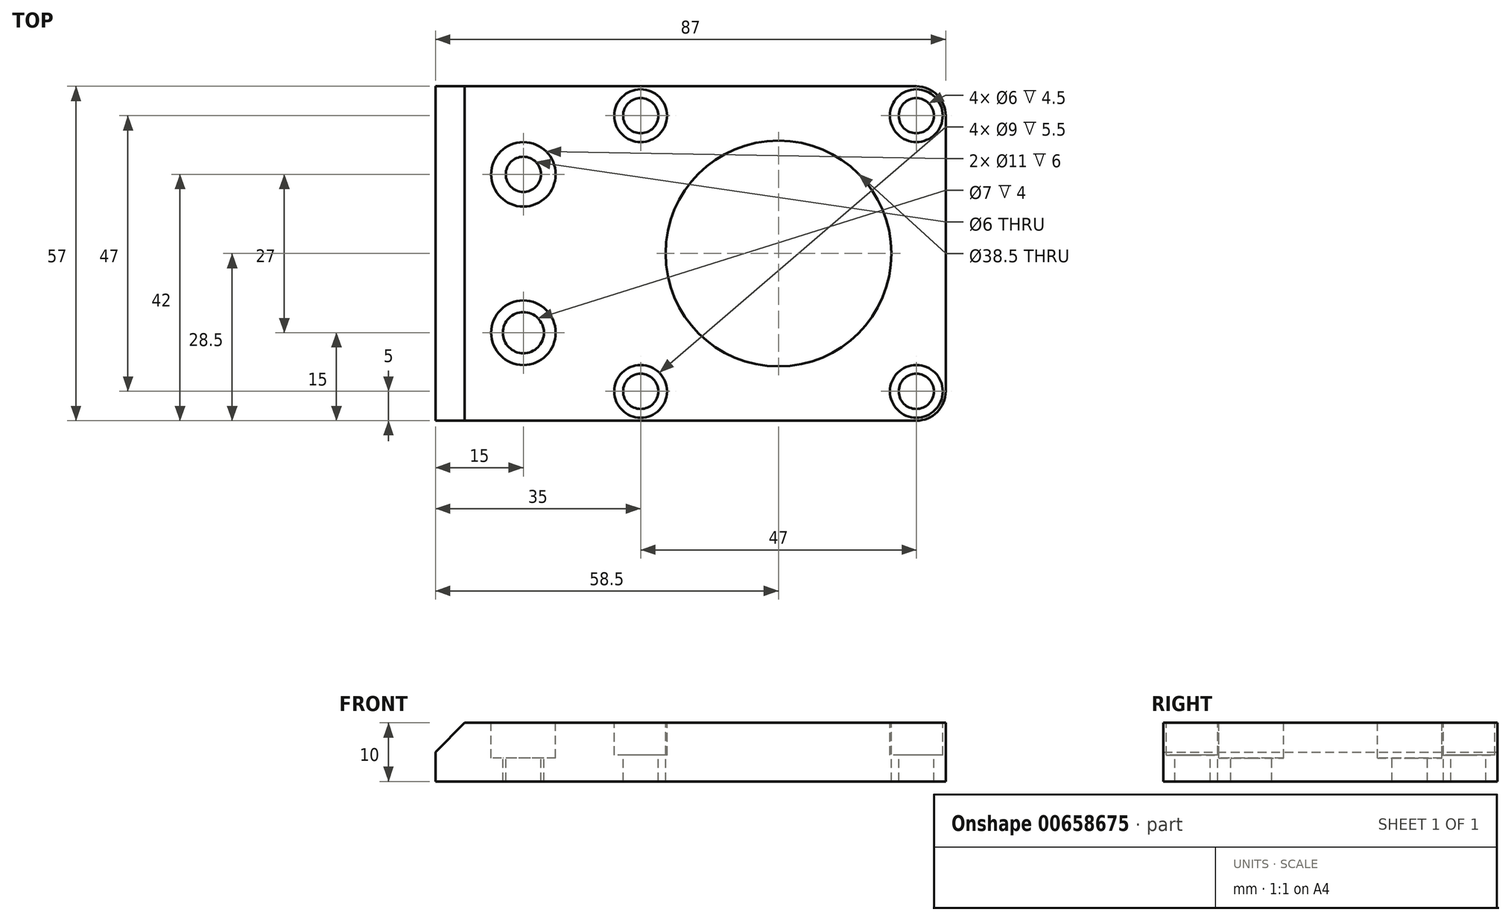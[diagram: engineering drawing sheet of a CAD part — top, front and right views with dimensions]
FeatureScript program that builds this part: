
annotation { "Feature Type Name" : "Feature", "Feature Type Description" : "" }
export const myFeature = defineFeature(function(context is Context, id is Id, definition is map)
    precondition{}
    {
        {
            var Q0;
            Q0=qCreatedBy(makeId("Top.planeOp"),FACE);
            var sketch = newSketch(context, id + "F0", { "sketchPlane" : qUnion([Q0])});
            skLineSegment(sketch, "E0.rect.bottom", {"start": v(43.5, -28.5) * mm, "end": v(-43.5, -28.5) * mm});
            skLineSegment(sketch, "E0.rect.top", {"start": v(43.5, 28.5) * mm, "end": v(-43.5, 28.5) * mm});
            skLineSegment(sketch, "E0.rect.left", {"start": v(43.5, -28.5) * mm, "end": v(43.5, 28.5) * mm});
            skLineSegment(sketch, "E0.rect.right", {"start": v(-43.5, -28.5) * mm, "end": v(-43.5, 28.5) * mm});
            skPoint(sketch, "E0.rect.middle", {"position": v(0, 0) * mm});
            skSolve(sketch);
        }
        {
            var Q0;
            Q0=makeQuery(id+"F0.imprint","IMPRINT",FACE,{"disambiguationData":[TD([[makeQuery(id+"F0.imprint","IMPRINT",EDGE,{"derivedFrom":sQuery(id+"F0.wireOp",EDGE,"E0.rect.bottom")}),-1.0]])]});
            extrude(context, id + "F1", {"entities" : qUnion([Q0]), "depth" : 10 * mm});
        }
        {
            var Q0;
            Q0=makeQuery(id+"F1.opExtrude","CAP_FACE",FACE,{"disambiguationData":[OSD([sQuery(id+"F0.wireOp",EDGE,"E0.rect.bottom"),sQuery(id+"F0.wireOp",EDGE,"E0.rect.top"),sQuery(id+"F0.wireOp",EDGE,"E0.rect.left"),sQuery(id+"F0.wireOp",EDGE,"E0.rect.right")])],"isStart":false});
            var sketch = newSketch(context, id + "F2", { "sketchPlane" : qUnion([Q0])});
            skCircle(sketch, "E1", {"center": v(15, 0) * mm, "radius": 19.25 * mm});
            skCircle(sketch, "E2", {"center": v(-28.5, -13.5) * mm, "radius": 3.5 * mm});
            skCircle(sketch, "E3", {"center": v(-28.5, 13.5) * mm, "radius": 3 * mm});
            skSolve(sketch);
        }
        {
            var Q0;
            Q0=makeQuery(id+"F2.imprint","IMPRINT",FACE,{"disambiguationData":[TD([[makeQuery(id+"F2.imprint","IMPRINT",EDGE,{"derivedFrom":sQuery(id+"F2.wireOp",EDGE,"E1")}),1.0]])]});
            var Q1;
            Q1=makeQuery(id+"F2.imprint","IMPRINT",FACE,{"disambiguationData":[TD([[makeQuery(id+"F2.imprint","IMPRINT",EDGE,{"derivedFrom":sQuery(id+"F2.wireOp",EDGE,"E3")}),1.0]])]});
            var Q2;
            Q2=makeQuery(id+"F2.imprint","IMPRINT",FACE,{"disambiguationData":[TD([[makeQuery(id+"F2.imprint","IMPRINT",EDGE,{"derivedFrom":sQuery(id+"F2.wireOp",EDGE,"E2")}),1.0]])]});
            extrude(context, id + "F3", {"entities" : qUnion([Q0, Q1, Q2]), "operationType" : NewBodyOperationType.REMOVE, "endBound" : BoundingType.THROUGH_ALL, "oppositeDirection" : true, "depth" : 25 * mm});
        }
        {
            var Q0;
            Q0=makeQuery(id+"F1.opExtrude","CAP_FACE",FACE,{"disambiguationData":[OSD([sQuery(id+"F0.wireOp",EDGE,"E0.rect.bottom"),sQuery(id+"F0.wireOp",EDGE,"E0.rect.top"),sQuery(id+"F0.wireOp",EDGE,"E0.rect.left"),sQuery(id+"F0.wireOp",EDGE,"E0.rect.right")])],"isStart":false});
            var sketch = newSketch(context, id + "F4", { "sketchPlane" : qUnion([Q0])});
            skPoint(sketch, "E4", {"position": v(-8.5, 23.5) * mm});
            skPoint(sketch, "E5", {"position": v(38.5, 23.5) * mm});
            skPoint(sketch, "E6", {"position": v(38.5, -23.5) * mm});
            skPoint(sketch, "E7", {"position": v(-8.5, -23.5) * mm});
            skSolve(sketch);
        }
        {
            var Q0;
            Q0=makeQuery(id+"F4.imprint","IMPRINT",FACE,{"disambiguationData":[TD([[makeQuery(id+"F4.imprint","IMPRINT",EDGE,{"derivedFrom":makeQuery(id+"F1.opExtrude","CAP_EDGE",EDGE,{"disambiguationData":[OSD([sQuery(id+"F0.wireOp",EDGE,"E0.rect.bottom")])],"isStart":false})}),-1.0]])]});
            var sketch = newSketch(context, id + "F5", { "sketchPlane" : qUnion([Q0])});
            skCircle(sketch, "E8.0", {"center": v(-28.5, 13.5) * mm, "radius": 3 * mm, "construction": true});
            skCircle(sketch, "E9.0", {"center": v(-28.5, -13.5) * mm, "radius": 3.5 * mm, "construction": true});
            skCircle(sketch, "E10", {"center": v(-28.5, 13.5) * mm, "radius": 5.5 * mm});
            skCircle(sketch, "E11", {"center": v(-28.5, -13.5) * mm, "radius": 5.5 * mm});
            skSolve(sketch);
        }
        {
            var Q0;
            Q0=qSketchRegion(id+"F5",true);
            extrude(context, id + "F6", {"entities" : qUnion([Q0]), "operationType" : NewBodyOperationType.REMOVE, "oppositeDirection" : true, "depth" : 6 * mm});
        }
        {
            var Q0;
            Q0=sQuery(id+"F4.wireOp",VERTEX,"E4");
            var Q1;
            Q1=sQuery(id+"F4.wireOp",VERTEX,"E5");
            var Q2;
            Q2=sQuery(id+"F4.wireOp",VERTEX,"E6");
            var Q3;
            Q3=sQuery(id+"F4.wireOp",VERTEX,"E7");
            var Q4;
            Q4=makeQuery(id+"F1.opExtrude","SWEPT_BODY",BODY,{"disambiguationData":[OSD([sQuery(id+"F0.wireOp",EDGE,"E0.rect.bottom"),sQuery(id+"F0.wireOp",EDGE,"E0.rect.top"),sQuery(id+"F0.wireOp",EDGE,"E0.rect.left"),sQuery(id+"F0.wireOp",EDGE,"E0.rect.right")])]});
            hole(context, id + "F7", {"style" : HoleStyle.C_BORE, "holeDiameter" : 6 * mm, "cBoreDiameter" : 9 * mm, "cBoreDepth" : 5.5 * mm, "endStyle" : HoleEndStyle.THROUGH, "locations" : qUnion([Q0, Q1, Q2, Q3]), "scope" : qUnion([Q4])});
        }
        {
            var Q0;
            Q0=makeQuery(id+"F1.opExtrude","SWEPT_EDGE",EDGE,{"disambiguationData":[OSD([sQuery(id+"F0.wireOp",EDGE,"E0.rect.bottom"),sQuery(id+"F0.wireOp",EDGE,"E0.rect.left")])]});
            var Q1;
            Q1=makeQuery(id+"F1.opExtrude","SWEPT_EDGE",EDGE,{"disambiguationData":[OSD([sQuery(id+"F0.wireOp",EDGE,"E0.rect.top"),sQuery(id+"F0.wireOp",EDGE,"E0.rect.left")])]});
            fillet(context, id + "F8", {"entities" : qUnion([Q0, Q1]), "radius" : 5 * mm, "tangentPropagation" : true, "allowEdgeOverflow" : false});
        }
        {
            var Q0;
            Q0=makeQuery(id+"F1.opExtrude","CAP_EDGE",EDGE,{"disambiguationData":[OSD([sQuery(id+"F0.wireOp",EDGE,"E0.rect.right")])],"isStart":false});
            chamfer(context, id + "F9", {"entities" : qUnion([Q0]), "width" : 5 * mm, "tangentPropagation" : true});
        }
    });
